# Revit family: NLRS_63_LF_UN_noodverlichting trendlux wand opbouw_hertek
name_source: partatom
category: Lighting Fixtures
units: mm (PartAtom-declared; Revit-internal decimal feet)

## family parameters
Always vertical = Yes
Cut with Voids When Loaded = No
Light Source = No
OmniClass Number = 23.85.30.21
OmniClass Title = Environmental Detection/Registration
Part Type = Normal
Room Calculation Point = No
Round Connector Dimension = Use Radius
Shared = No
Work Plane-Based = No

## types (1)
- Trendlux Series 3 dec AT opbouw wand - vluchtwegaanduiding_htk_NTD210-4
    Apparent Load = 6 VA
    Default Elevation = 0 mm  [stored 0 ft]
    Lamp = LED
    Manufacturer = Hertek
    NLRS_C_breedte = 90 mm
    NLRS_C_code_artikel = NTD210-4
    NLRS_C_code_fabrikant_gln = 8714253082646
    NLRS_C_hoogte = 170 mm  [stored 0.557743 ft]
    NLRS_C_lengte = 370 mm  [stored 1.21391 ft]
    NLRS_C_materiaal = Polycarbonaat wit
    NLRS_C_materiaal_01 = Glass
    NLRS_C_materiaal_kleur = wit
    NLRS_C_model = Trendlux Series 3 dec AT opbouw LiFePo4 10/8YW
    NLRS_C_omschrijving = Trendlux Series 3 dec AT opbouw LiFePo4 10/8YW
    NLRS_C_revit_versie = 2020
    NLRS_E_c01_radius = 8 mm  [stored 0.0262467 ft]
    NLRS_E_c01_schijnbaar_vermogen = 6 VA
    NLRS_E_c01_schijnbaar_vermogen_fase_1 = 0 VA
    NLRS_E_c01_schijnbaar_vermogen_fase_2 = 0 VA
    NLRS_E_c01_schijnbaar_vermogen_fase_3 = 0 VA
    NLRS_E_spanning = 230 V
    NLRS_E_stroom = 0.0 A
    NLRS_S_gewicht_netto = 0.00 kg
    URL = www.hertek.eu
    Wattage Comments = 2-6W (dimbaar)
    batterij = LiFePo4
    centraal = No
    decentraal = Yes
    picto = No
    plafondmontage = No
    vermogensclassificatie = NV
    wireless = No
    zichtbaar_01 = No

note: [stored X ft] marks values corroborated as IEEE doubles in the binary element streams (Revit-internal decimal feet)

## geometry (parser evidence)
native form markers: Blend x12, Sweep x35
no freeform markers — native parametric forms only
